# Revit family: Nivellierbare Kassette für Revisionsöffnung, RKN
name_source: partatom
category: Generic Models
revit_build: Autodesk Revit 2015 (Build: 20140606_1530(x64)
units: mm (PartAtom-declared; Revit-internal decimal feet)

## types (2) — shared parameters
Cut depth = 20 mm  [stored 0.0656168 ft]
Height = 150 mm
Height 1 = 29 mm  [stored 0.0951444 ft]
HeightCalc = 150 mm
Length = 199 mm  [stored 0.652887 ft]
Manufacturer = OBO Bettermann
URL = http://www.obo-bettermann.com
Width = 199 mm  [stored 0.652887 ft]

## per-type parameters (varying)
| type | GTIN | Manufacturer Art.No. | Material |
| RKN2 4 VS 20 | 4012195867531 | 7409014 | Stainless Steel, Polished |
| RKN2 4 MS 20 | 4012195867340 | 7409002 | Brass, Soft Yellow, Welded |

note: column(s) folded — value = type name in every type: Article Type

note: [stored X ft] marks values corroborated as IEEE doubles in the binary element streams (Revit-internal decimal feet)

## geometry (parser evidence)
native form markers: Sweep x2
no freeform markers — native parametric forms only
